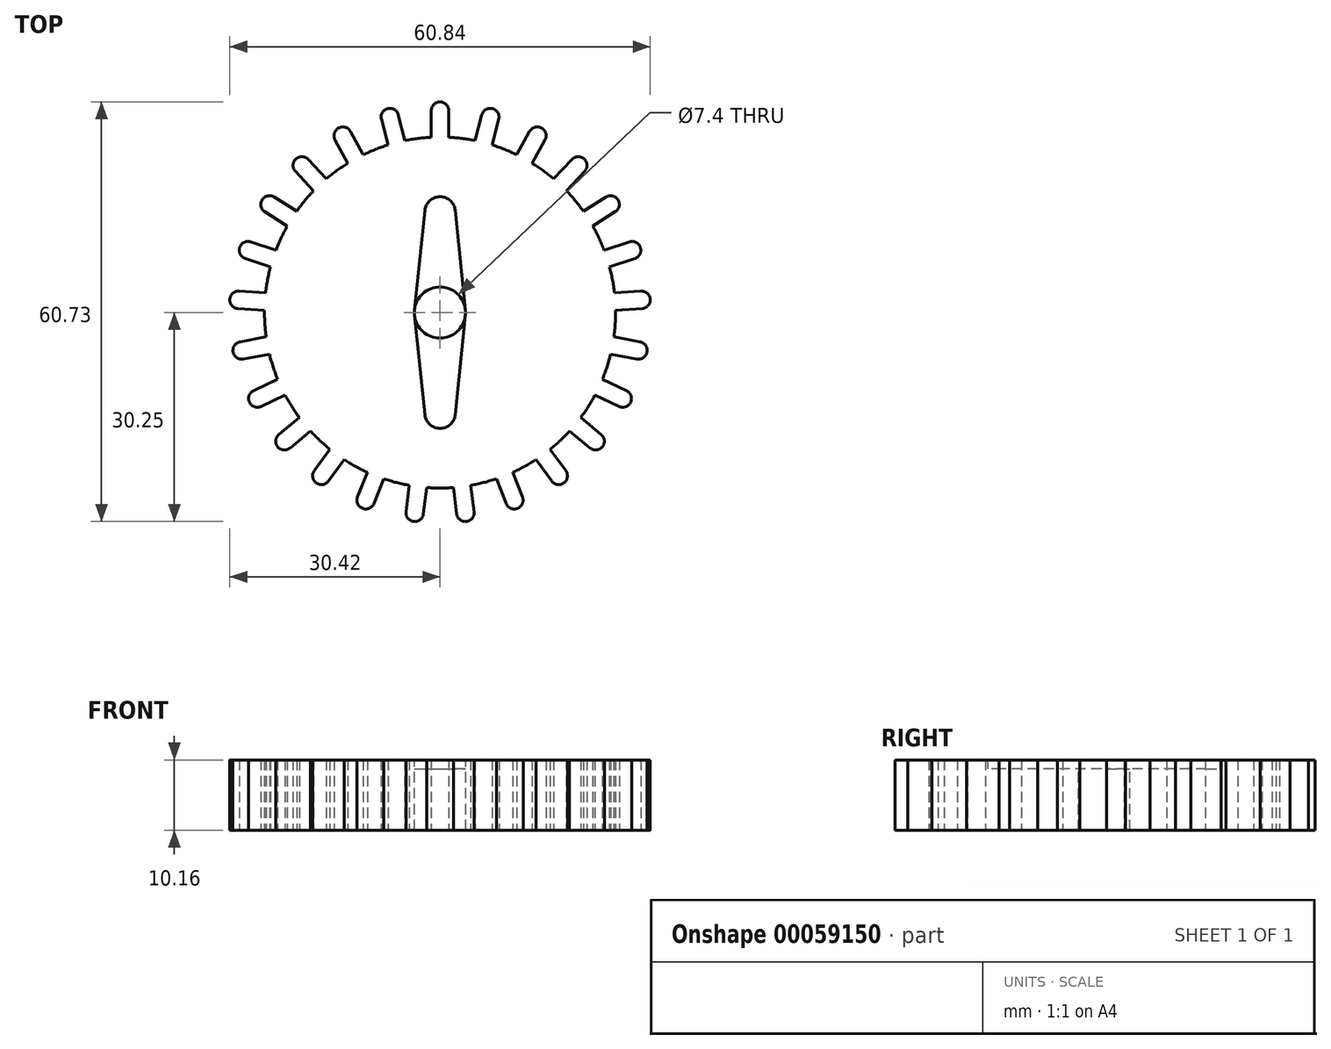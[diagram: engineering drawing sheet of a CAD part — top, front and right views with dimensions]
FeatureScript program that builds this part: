
annotation { "Feature Type Name" : "Feature", "Feature Type Description" : "" }
export const myFeature = defineFeature(function(context is Context, id is Id, definition is map)
    precondition{}
    {
        {
            var Q0;
            Q0=qCreatedBy(makeId("Top.planeOp"),FACE);
            var sketch = newSketch(context, id + "F0", { "sketchPlane" : qUnion([Q0])});
            skCircle(sketch, "E0", {"center": v(0, 0) * mm, "radius": 25.4 * mm});
            skLineSegment(sketch, "E1", {"start": v(-1.27, 29.21) * mm, "end": v(-1.27, 25.37) * mm});
            skLineSegment(sketch, "E2", {"start": v(1.27, 29.21) * mm, "end": v(1.27, 25.37) * mm});
            skArc(sketch, "E3", {"start": v(1.27, 29.21) * mm, "mid": v(0, 30.48) * mm, "end": v(-1.27, 29.21) * mm});
            skLineSegment(sketch, "E4.1.0", {"start": v(-8.5, 27.98) * mm, "end": v(-7.54, 24.26) * mm});
            skLineSegment(sketch, "E4.1.1", {"start": v(-6.03, 28.6) * mm, "end": v(-5.08, 24.89) * mm});
            skArc(sketch, "E4.1.2", {"start": v(-6.03, 28.6) * mm, "mid": v(-7.58, 29.52) * mm, "end": v(-8.5, 27.98) * mm});
            skLineSegment(sketch, "E4.2.0", {"start": v(-15.18, 24.99) * mm, "end": v(-13.33, 21.62) * mm});
            skLineSegment(sketch, "E4.2.1", {"start": v(-12.96, 26.2) * mm, "end": v(-11.1, 22.84) * mm});
            skArc(sketch, "E4.2.2", {"start": v(-12.96, 26.2) * mm, "mid": v(-14.68, 26.7) * mm, "end": v(-15.18, 24.99) * mm});
            skLineSegment(sketch, "E4.3.0", {"start": v(-20.92, 20.42) * mm, "end": v(-18.3, 17.62) * mm});
            skLineSegment(sketch, "E4.3.1", {"start": v(-19.07, 22.16) * mm, "end": v(-16.44, 19.36) * mm});
            skArc(sketch, "E4.3.2", {"start": v(-19.07, 22.16) * mm, "mid": v(-20.86, 22.22) * mm, "end": v(-20.92, 20.42) * mm});
            skLineSegment(sketch, "E4.4.0", {"start": v(-25.34, 14.58) * mm, "end": v(-22.1, 12.52) * mm});
            skLineSegment(sketch, "E4.4.1", {"start": v(-23.98, 16.72) * mm, "end": v(-20.74, 14.67) * mm});
            skArc(sketch, "E4.4.2", {"start": v(-23.98, 16.72) * mm, "mid": v(-25.74, 16.33) * mm, "end": v(-25.34, 14.58) * mm});
            skLineSegment(sketch, "E4.5.0", {"start": v(-28.17, 7.82) * mm, "end": v(-24.52, 6.63) * mm});
            skLineSegment(sketch, "E4.5.1", {"start": v(-27.39, 10.23) * mm, "end": v(-23.73, 9.05) * mm});
            skArc(sketch, "E4.5.2", {"start": v(-27.39, 10.23) * mm, "mid": v(-28.99, 9.42) * mm, "end": v(-28.17, 7.82) * mm});
            skLineSegment(sketch, "E4.6.0", {"start": v(-29.23, 0.57) * mm, "end": v(-25.4, 0.33) * mm});
            skLineSegment(sketch, "E4.6.1", {"start": v(-29.07, 3.1) * mm, "end": v(-25.24, 2.86) * mm});
            skArc(sketch, "E4.6.2", {"start": v(-29.07, 3.1) * mm, "mid": v(-30.42, 1.91) * mm, "end": v(-29.23, 0.57) * mm});
            skLineSegment(sketch, "E4.7.0", {"start": v(-28.45, -6.72) * mm, "end": v(-24.68, -6) * mm});
            skLineSegment(sketch, "E4.7.1", {"start": v(-28.93, -4.23) * mm, "end": v(-25.16, -3.5) * mm});
            skArc(sketch, "E4.7.2", {"start": v(-28.93, -4.23) * mm, "mid": v(-29.94, -5.71) * mm, "end": v(-28.45, -6.72) * mm});
            skLineSegment(sketch, "E4.8.0", {"start": v(-25.89, -13.59) * mm, "end": v(-22.41, -11.95) * mm});
            skLineSegment(sketch, "E4.8.1", {"start": v(-26.97, -11.29) * mm, "end": v(-23.5, -9.65) * mm});
            skArc(sketch, "E4.8.2", {"start": v(-26.97, -11.29) * mm, "mid": v(-27.58, -12.98) * mm, "end": v(-25.89, -13.59) * mm});
            skLineSegment(sketch, "E4.9.0", {"start": v(-21.7, -19.6) * mm, "end": v(-18.74, -17.15) * mm});
            skLineSegment(sketch, "E4.9.1", {"start": v(-23.32, -17.64) * mm, "end": v(-20.36, -15.2) * mm});
            skArc(sketch, "E4.9.2", {"start": v(-23.32, -17.64) * mm, "mid": v(-23.49, -19.43) * mm, "end": v(-21.7, -19.6) * mm});
            skLineSegment(sketch, "E4.10.0", {"start": v(-16.14, -24.38) * mm, "end": v(-13.88, -21.27) * mm});
            skLineSegment(sketch, "E4.10.1", {"start": v(-18.2, -22.88) * mm, "end": v(-15.94, -19.78) * mm});
            skArc(sketch, "E4.10.2", {"start": v(-18.2, -22.88) * mm, "mid": v(-17.92, -24.66) * mm, "end": v(-16.14, -24.38) * mm});
            skLineSegment(sketch, "E4.11.0", {"start": v(-9.57, -27.63) * mm, "end": v(-8.16, -24.05) * mm});
            skLineSegment(sketch, "E4.11.1", {"start": v(-11.93, -26.7) * mm, "end": v(-10.52, -23.12) * mm});
            skArc(sketch, "E4.11.2", {"start": v(-11.93, -26.7) * mm, "mid": v(-11.22, -28.34) * mm, "end": v(-9.57, -27.63) * mm});
            skLineSegment(sketch, "E4.12.0", {"start": v(-2.4, -29.14) * mm, "end": v(-1.92, -25.33) * mm});
            skLineSegment(sketch, "E4.12.1", {"start": v(-4.92, -28.82) * mm, "end": v(-4.44, -25) * mm});
            skArc(sketch, "E4.12.2", {"start": v(-4.92, -28.82) * mm, "mid": v(-3.82, -30.24) * mm, "end": v(-2.4, -29.14) * mm});
            skLineSegment(sketch, "E4.13.0", {"start": v(4.92, -28.82) * mm, "end": v(4.44, -25) * mm});
            skLineSegment(sketch, "E4.13.1", {"start": v(2.4, -29.14) * mm, "end": v(1.92, -25.33) * mm});
            skArc(sketch, "E4.13.2", {"start": v(2.4, -29.14) * mm, "mid": v(3.82, -30.24) * mm, "end": v(4.92, -28.82) * mm});
            skLineSegment(sketch, "E4.14.0", {"start": v(11.93, -26.7) * mm, "end": v(10.52, -23.12) * mm});
            skLineSegment(sketch, "E4.14.1", {"start": v(9.57, -27.63) * mm, "end": v(8.16, -24.05) * mm});
            skArc(sketch, "E4.14.2", {"start": v(9.57, -27.63) * mm, "mid": v(11.22, -28.34) * mm, "end": v(11.93, -26.7) * mm});
            skLineSegment(sketch, "E4.15.0", {"start": v(18.2, -22.88) * mm, "end": v(15.94, -19.78) * mm});
            skLineSegment(sketch, "E4.15.1", {"start": v(16.14, -24.38) * mm, "end": v(13.88, -21.27) * mm});
            skArc(sketch, "E4.15.2", {"start": v(16.14, -24.38) * mm, "mid": v(17.92, -24.66) * mm, "end": v(18.2, -22.88) * mm});
            skLineSegment(sketch, "E4.16.0", {"start": v(23.32, -17.64) * mm, "end": v(20.36, -15.2) * mm});
            skLineSegment(sketch, "E4.16.1", {"start": v(21.7, -19.6) * mm, "end": v(18.74, -17.15) * mm});
            skArc(sketch, "E4.16.2", {"start": v(21.7, -19.6) * mm, "mid": v(23.49, -19.43) * mm, "end": v(23.32, -17.64) * mm});
            skLineSegment(sketch, "E4.17.0", {"start": v(26.97, -11.29) * mm, "end": v(23.5, -9.65) * mm});
            skLineSegment(sketch, "E4.17.1", {"start": v(25.89, -13.59) * mm, "end": v(22.41, -11.95) * mm});
            skArc(sketch, "E4.17.2", {"start": v(25.89, -13.59) * mm, "mid": v(27.58, -12.98) * mm, "end": v(26.97, -11.29) * mm});
            skLineSegment(sketch, "E4.18.0", {"start": v(28.93, -4.23) * mm, "end": v(25.16, -3.5) * mm});
            skLineSegment(sketch, "E4.18.1", {"start": v(28.45, -6.72) * mm, "end": v(24.68, -6) * mm});
            skArc(sketch, "E4.18.2", {"start": v(28.45, -6.72) * mm, "mid": v(29.94, -5.71) * mm, "end": v(28.93, -4.23) * mm});
            skLineSegment(sketch, "E4.19.0", {"start": v(29.07, 3.1) * mm, "end": v(25.24, 2.86) * mm});
            skLineSegment(sketch, "E4.19.1", {"start": v(29.23, 0.57) * mm, "end": v(25.4, 0.33) * mm});
            skArc(sketch, "E4.19.2", {"start": v(29.23, 0.57) * mm, "mid": v(30.42, 1.91) * mm, "end": v(29.07, 3.1) * mm});
            skLineSegment(sketch, "E4.20.0", {"start": v(27.39, 10.23) * mm, "end": v(23.73, 9.05) * mm});
            skLineSegment(sketch, "E4.20.1", {"start": v(28.17, 7.82) * mm, "end": v(24.52, 6.63) * mm});
            skArc(sketch, "E4.20.2", {"start": v(28.17, 7.82) * mm, "mid": v(28.99, 9.42) * mm, "end": v(27.39, 10.23) * mm});
            skLineSegment(sketch, "E4.21.0", {"start": v(23.98, 16.72) * mm, "end": v(20.74, 14.67) * mm});
            skLineSegment(sketch, "E4.21.1", {"start": v(25.34, 14.58) * mm, "end": v(22.1, 12.52) * mm});
            skArc(sketch, "E4.21.2", {"start": v(25.34, 14.58) * mm, "mid": v(25.74, 16.33) * mm, "end": v(23.98, 16.72) * mm});
            skLineSegment(sketch, "E4.22.0", {"start": v(19.07, 22.16) * mm, "end": v(16.44, 19.36) * mm});
            skLineSegment(sketch, "E4.22.1", {"start": v(20.92, 20.42) * mm, "end": v(18.3, 17.62) * mm});
            skArc(sketch, "E4.22.2", {"start": v(20.92, 20.42) * mm, "mid": v(20.86, 22.22) * mm, "end": v(19.07, 22.16) * mm});
            skLineSegment(sketch, "E4.23.0", {"start": v(12.96, 26.2) * mm, "end": v(11.1, 22.84) * mm});
            skLineSegment(sketch, "E4.23.1", {"start": v(15.18, 24.99) * mm, "end": v(13.33, 21.62) * mm});
            skArc(sketch, "E4.23.2", {"start": v(15.18, 24.99) * mm, "mid": v(14.68, 26.7) * mm, "end": v(12.96, 26.2) * mm});
            skLineSegment(sketch, "E5.2.24.0", {"start": v(6.03, 28.6) * mm, "end": v(5.08, 24.89) * mm});
            skLineSegment(sketch, "E5.3.24.0", {"start": v(8.5, 27.98) * mm, "end": v(7.54, 24.26) * mm});
            skArc(sketch, "E5.6.24.0", {"start": v(8.5, 27.98) * mm, "mid": v(7.58, 29.52) * mm, "end": v(6.03, 28.6) * mm});
            skSolve(sketch);
        }
        {
            var Q0;
            Q0 = qSketchRegion(id + "F0", true);
            extrude(context, id + "F1", {"entities" : qUnion([Q0]), "depth" : 10.16 * mm});
        }
        {
            var Q0;
            Q0=makeQuery(id+"F1.opExtrude","CAP_FACE",FACE,{"disambiguationData":[OSD([sQuery(id+"F0.wireOp",EDGE,"E0"),sQuery(id+"F0.wireOp",EDGE,"E1"),sQuery(id+"F0.wireOp",EDGE,"E2"),sQuery(id+"F0.wireOp",EDGE,"E3"),sQuery(id+"F0.wireOp",EDGE,"2d6da723-643c-446d-b98c-e9a23709f50f.1.0"),sQuery(id+"F0.wireOp",EDGE,"2d6da723-643c-446d-b98c-e9a23709f50f.1.1"),sQuery(id+"F0.wireOp",EDGE,"2d6da723-643c-446d-b98c-e9a23709f50f.1.2"),sQuery(id+"F0.wireOp",EDGE,"2d6da723-643c-446d-b98c-e9a23709f50f.2.0"),sQuery(id+"F0.wireOp",EDGE,"2d6da723-643c-446d-b98c-e9a23709f50f.2.1"),sQuery(id+"F0.wireOp",EDGE,"2d6da723-643c-446d-b98c-e9a23709f50f.2.2"),sQuery(id+"F0.wireOp",EDGE,"2d6da723-643c-446d-b98c-e9a23709f50f.3.0"),sQuery(id+"F0.wireOp",EDGE,"2d6da723-643c-446d-b98c-e9a23709f50f.3.1"),sQuery(id+"F0.wireOp",EDGE,"2d6da723-643c-446d-b98c-e9a23709f50f.3.2"),sQuery(id+"F0.wireOp",EDGE,"2d6da723-643c-446d-b98c-e9a23709f50f.4.0"),sQuery(id+"F0.wireOp",EDGE,"2d6da723-643c-446d-b98c-e9a23709f50f.4.1"),sQuery(id+"F0.wireOp",EDGE,"2d6da723-643c-446d-b98c-e9a23709f50f.4.2"),sQuery(id+"F0.wireOp",EDGE,"2d6da723-643c-446d-b98c-e9a23709f50f.5.0"),sQuery(id+"F0.wireOp",EDGE,"2d6da723-643c-446d-b98c-e9a23709f50f.5.1"),sQuery(id+"F0.wireOp",EDGE,"2d6da723-643c-446d-b98c-e9a23709f50f.5.2"),sQuery(id+"F0.wireOp",EDGE,"2d6da723-643c-446d-b98c-e9a23709f50f.6.0"),sQuery(id+"F0.wireOp",EDGE,"2d6da723-643c-446d-b98c-e9a23709f50f.6.1"),sQuery(id+"F0.wireOp",EDGE,"2d6da723-643c-446d-b98c-e9a23709f50f.6.2"),sQuery(id+"F0.wireOp",EDGE,"2d6da723-643c-446d-b98c-e9a23709f50f.7.0"),sQuery(id+"F0.wireOp",EDGE,"2d6da723-643c-446d-b98c-e9a23709f50f.7.1"),sQuery(id+"F0.wireOp",EDGE,"2d6da723-643c-446d-b98c-e9a23709f50f.7.2"),sQuery(id+"F0.wireOp",EDGE,"2d6da723-643c-446d-b98c-e9a23709f50f.8.0"),sQuery(id+"F0.wireOp",EDGE,"2d6da723-643c-446d-b98c-e9a23709f50f.8.1"),sQuery(id+"F0.wireOp",EDGE,"2d6da723-643c-446d-b98c-e9a23709f50f.8.2"),sQuery(id+"F0.wireOp",EDGE,"2d6da723-643c-446d-b98c-e9a23709f50f.9.0"),sQuery(id+"F0.wireOp",EDGE,"2d6da723-643c-446d-b98c-e9a23709f50f.9.1"),sQuery(id+"F0.wireOp",EDGE,"2d6da723-643c-446d-b98c-e9a23709f50f.9.2"),sQuery(id+"F0.wireOp",EDGE,"2d6da723-643c-446d-b98c-e9a23709f50f.10.0"),sQuery(id+"F0.wireOp",EDGE,"2d6da723-643c-446d-b98c-e9a23709f50f.10.1"),sQuery(id+"F0.wireOp",EDGE,"2d6da723-643c-446d-b98c-e9a23709f50f.10.2"),sQuery(id+"F0.wireOp",EDGE,"2d6da723-643c-446d-b98c-e9a23709f50f.11.0"),sQuery(id+"F0.wireOp",EDGE,"2d6da723-643c-446d-b98c-e9a23709f50f.11.1"),sQuery(id+"F0.wireOp",EDGE,"2d6da723-643c-446d-b98c-e9a23709f50f.11.2"),sQuery(id+"F0.wireOp",EDGE,"2d6da723-643c-446d-b98c-e9a23709f50f.12.0"),sQuery(id+"F0.wireOp",EDGE,"2d6da723-643c-446d-b98c-e9a23709f50f.12.1"),sQuery(id+"F0.wireOp",EDGE,"2d6da723-643c-446d-b98c-e9a23709f50f.12.2"),sQuery(id+"F0.wireOp",EDGE,"2d6da723-643c-446d-b98c-e9a23709f50f.13.0"),sQuery(id+"F0.wireOp",EDGE,"2d6da723-643c-446d-b98c-e9a23709f50f.13.1"),sQuery(id+"F0.wireOp",EDGE,"2d6da723-643c-446d-b98c-e9a23709f50f.13.2"),sQuery(id+"F0.wireOp",EDGE,"2d6da723-643c-446d-b98c-e9a23709f50f.14.0"),sQuery(id+"F0.wireOp",EDGE,"2d6da723-643c-446d-b98c-e9a23709f50f.14.1"),sQuery(id+"F0.wireOp",EDGE,"2d6da723-643c-446d-b98c-e9a23709f50f.14.2"),sQuery(id+"F0.wireOp",EDGE,"2d6da723-643c-446d-b98c-e9a23709f50f.15.0"),sQuery(id+"F0.wireOp",EDGE,"2d6da723-643c-446d-b98c-e9a23709f50f.15.1"),sQuery(id+"F0.wireOp",EDGE,"2d6da723-643c-446d-b98c-e9a23709f50f.15.2"),sQuery(id+"F0.wireOp",EDGE,"2d6da723-643c-446d-b98c-e9a23709f50f.16.0"),sQuery(id+"F0.wireOp",EDGE,"2d6da723-643c-446d-b98c-e9a23709f50f.16.1"),sQuery(id+"F0.wireOp",EDGE,"2d6da723-643c-446d-b98c-e9a23709f50f.16.2"),sQuery(id+"F0.wireOp",EDGE,"2d6da723-643c-446d-b98c-e9a23709f50f.17.0"),sQuery(id+"F0.wireOp",EDGE,"2d6da723-643c-446d-b98c-e9a23709f50f.17.1"),sQuery(id+"F0.wireOp",EDGE,"2d6da723-643c-446d-b98c-e9a23709f50f.17.2"),sQuery(id+"F0.wireOp",EDGE,"2d6da723-643c-446d-b98c-e9a23709f50f.18.0"),sQuery(id+"F0.wireOp",EDGE,"2d6da723-643c-446d-b98c-e9a23709f50f.18.1"),sQuery(id+"F0.wireOp",EDGE,"2d6da723-643c-446d-b98c-e9a23709f50f.18.2"),sQuery(id+"F0.wireOp",EDGE,"2d6da723-643c-446d-b98c-e9a23709f50f.19.0"),sQuery(id+"F0.wireOp",EDGE,"2d6da723-643c-446d-b98c-e9a23709f50f.19.1"),sQuery(id+"F0.wireOp",EDGE,"2d6da723-643c-446d-b98c-e9a23709f50f.19.2"),sQuery(id+"F0.wireOp",EDGE,"6e91e605-a990-4f15-ab5d-784bec117bc0.2.20.0"),sQuery(id+"F0.wireOp",EDGE,"6e91e605-a990-4f15-ab5d-784bec117bc0.3.20.0"),sQuery(id+"F0.wireOp",EDGE,"6e91e605-a990-4f15-ab5d-784bec117bc0.6.20.0"),sQuery(id+"F0.wireOp",EDGE,"6e91e605-a990-4f15-ab5d-784bec117bc0.2.21.0"),sQuery(id+"F0.wireOp",EDGE,"6e91e605-a990-4f15-ab5d-784bec117bc0.3.21.0"),sQuery(id+"F0.wireOp",EDGE,"6e91e605-a990-4f15-ab5d-784bec117bc0.6.21.0"),sQuery(id+"F0.wireOp",EDGE,"8e6adc96-cb9b-4fac-b7ac-7b12663be43e.2.22.0"),sQuery(id+"F0.wireOp",EDGE,"8e6adc96-cb9b-4fac-b7ac-7b12663be43e.3.22.0"),sQuery(id+"F0.wireOp",EDGE,"8e6adc96-cb9b-4fac-b7ac-7b12663be43e.6.22.0"),sQuery(id+"F0.wireOp",EDGE,"8e6adc96-cb9b-4fac-b7ac-7b12663be43e.2.23.0"),sQuery(id+"F0.wireOp",EDGE,"8e6adc96-cb9b-4fac-b7ac-7b12663be43e.3.23.0"),sQuery(id+"F0.wireOp",EDGE,"8e6adc96-cb9b-4fac-b7ac-7b12663be43e.6.23.0"),sQuery(id+"F0.wireOp",EDGE,"8e6adc96-cb9b-4fac-b7ac-7b12663be43e.2.24.0"),sQuery(id+"F0.wireOp",EDGE,"8e6adc96-cb9b-4fac-b7ac-7b12663be43e.3.24.0"),sQuery(id+"F0.wireOp",EDGE,"8e6adc96-cb9b-4fac-b7ac-7b12663be43e.6.24.0")])],"isStart":false});
            var sketch = newSketch(context, id + "F2", { "sketchPlane" : qUnion([Q0])});
            skLineSegment(sketch, "E6", {"start": v(3.68, -0.38) * mm, "end": v(2.2, -14.78) * mm});
            skLineSegment(sketch, "E7", {"start": v(-3.68, -0.38) * mm, "end": v(-2.2, -14.78) * mm});
            skLineSegment(sketch, "E8", {"start": v(2.2, 14.78) * mm, "end": v(3.68, 0.38) * mm});
            skLineSegment(sketch, "E9", {"start": v(-3.68, 0.38) * mm, "end": v(-2.2, 14.78) * mm});
            skCircle(sketch, "E10", {"center": v(0, 0) * mm, "radius": 3.7 * mm});
            skArc(sketch, "E11", {"start": v(2.2, 14.78) * mm, "mid": v(0, 16.76) * mm, "end": v(-2.2, 14.78) * mm});
            skArc(sketch, "E12", {"start": v(-2.2, -14.78) * mm, "mid": v(0, -16.76) * mm, "end": v(2.2, -14.78) * mm});
            skSolve(sketch);
        }
        {
            var Q0;
            {var subQ0=sQuery(id+"F2.wireOp",EDGE,"E8");Q0=makeQuery(id+"F2.imprint","IMPRINT",FACE,{"disambiguationData":[TD([[makeQuery(id+"F2.imprint","IMPRINT",EDGE,{"derivedFrom":subQ0}),-1.0]])]});}
            var Q1;
            {var subQ0=sQuery(id+"F2.wireOp",EDGE,"E6");Q1=makeQuery(id+"F2.imprint","IMPRINT",FACE,{"disambiguationData":[TD([[makeQuery(id+"F2.imprint","IMPRINT",EDGE,{"derivedFrom":subQ0}),-1.0]])]});}
            extrude(context, id + "F3", {"entities" : qUnion([Q0, Q1]), "operationType" : NewBodyOperationType.REMOVE, "oppositeDirection" : true, "depth" : 1.27 * mm});
        }
        {
            var Q0;
            {var subQ0=sQuery(id+"F2.wireOp",EDGE,"E10");var subQ1=makeQuery(id+"F2.imprint","INTERSECT",VERTEX,{"derivedFrom":[sQuery(id+"F2.wireOp",EDGE,"E8"),subQ0]});Q0=makeQuery(id+"F2.imprint","IMPRINT",FACE,{"disambiguationData":[TD([[makeQuery(id+"F2.imprint","IMPRINT",EDGE,{"disambiguationData":[TD([[subQ1,-1.0]])],"derivedFrom":subQ0}),1.0]])]});}
            extrude(context, id + "F4", {"entities" : qUnion([Q0]), "operationType" : NewBodyOperationType.REMOVE, "oppositeDirection" : true, "depth" : 25.4 * mm});
        }
    });
